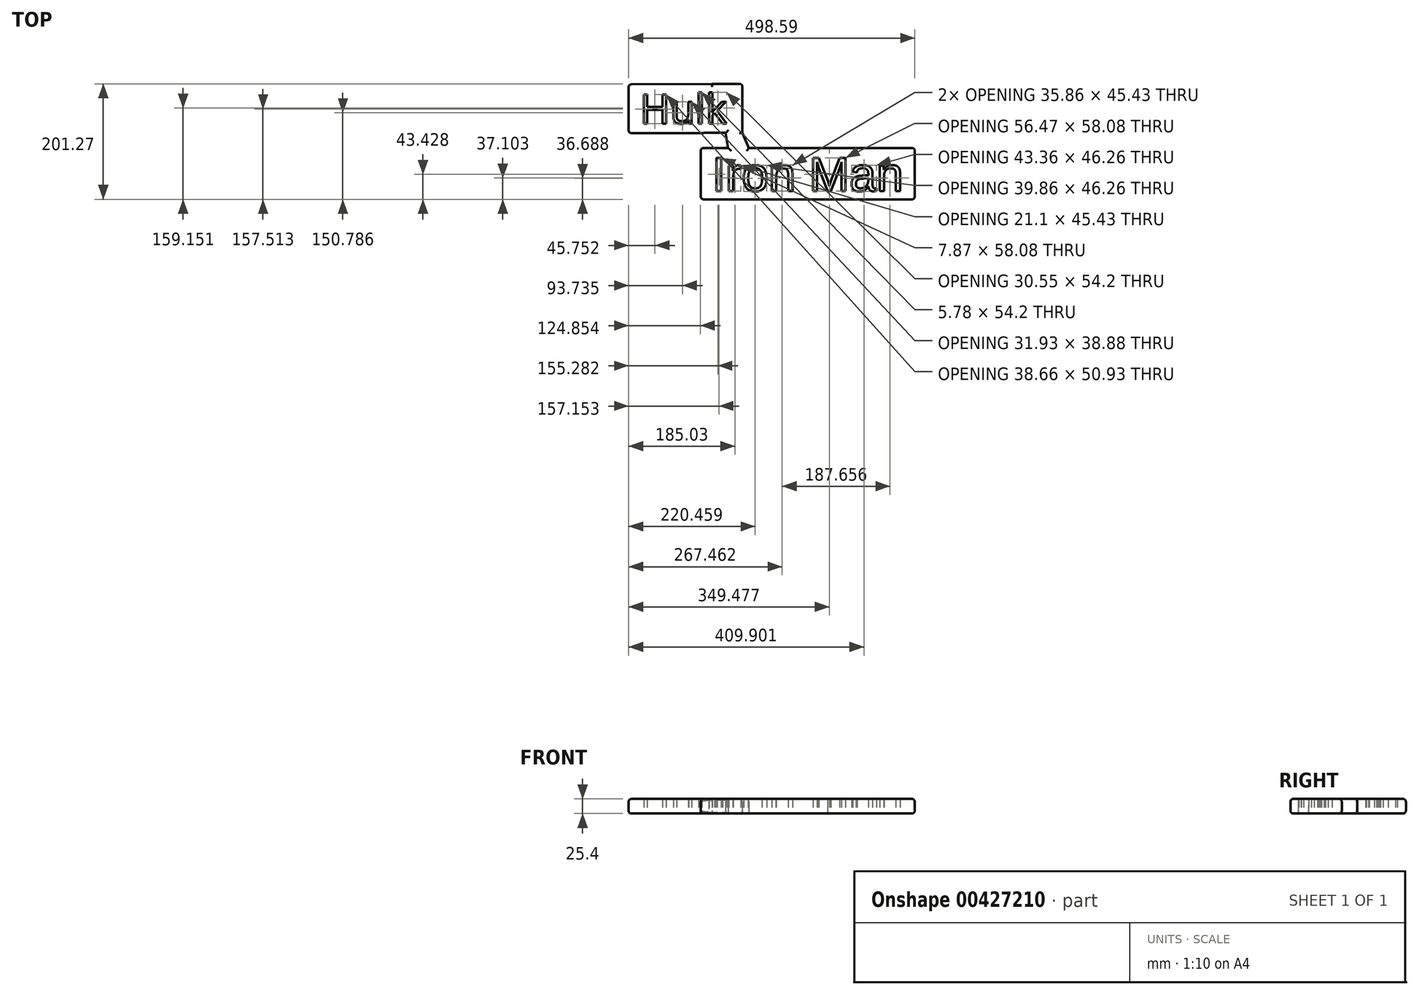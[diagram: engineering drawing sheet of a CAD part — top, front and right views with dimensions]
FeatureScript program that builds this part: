
annotation { "Feature Type Name" : "Feature", "Feature Type Description" : "" }
export const myFeature = defineFeature(function(context is Context, id is Id, definition is map)
    precondition{}
    {
        {
            var Q0;
            Q0=qCreatedBy(makeId("Top.planeOp"),FACE);
            var sketch = newSketch(context, id + "F0", { "sketchPlane" : qUnion([Q0])});
            skLineSegment(sketch, "E0", {"start": v(68.88, -39.62) * mm, "end": v(-56.84, -39.62) * mm});
            skLineSegment(sketch, "E1", {"start": v(-56.84, -39.62) * mm, "end": v(-56.84, 45.43) * mm});
            skLineSegment(sketch, "E2", {"start": v(-56.84, 45.43) * mm, "end": v(88.58, 46.24) * mm});
            skText(sketch, "E3", { "text": "Iron Man", "fontName": "Arimo-Regular.ttf"});
            skPoint(sketch, "E3.firstSnap0", {"position": v(88.58, 46.24) * mm});
            skPoint(sketch, "E4.end.orphan", {"position": v(326.73, 0) * mm});
            skLineSegment(sketch, "E5", {"start": v(295.08, 47.04) * mm, "end": v(296.03, 47.04) * mm});
            skText(sketch, "E6", { "text": "Hulk", "fontName": "OpenSans-Regular.ttf"});
            skPoint(sketch, "E7.start.orphan", {"position": v(234, 47.04) * mm});
            skLineSegment(sketch, "E8", {"start": v(88.58, 46.24) * mm, "end": v(141.43, 46.24) * mm});
            skLineSegment(sketch, "E9", {"start": v(141.43, 46.24) * mm, "end": v(141.43, -38.79) * mm});
            skLineSegment(sketch, "E10", {"start": v(141.43, -38.79) * mm, "end": v(82.89, -38.79) * mm});
            skLineSegment(sketch, "E11", {"start": v(68.88, -39.62) * mm, "end": v(82.89, -38.79) * mm});
            skLineSegment(sketch, "E12", {"start": v(112.16, -38.79) * mm, "end": v(118.33, -79.87) * mm});
            skLineSegment(sketch, "E13", {"start": v(118.33, -79.87) * mm, "end": v(141.43, -38.79) * mm});
            skLineSegment(sketch, "E14", {"start": v(141.43, -38.79) * mm, "end": v(158.58, -79.87) * mm});
            skLineSegment(sketch, "E15.bottom", {"start": v(68.88, -65.48) * mm, "end": v(441.75, -65.48) * mm});
            skLineSegment(sketch, "E15.top", {"start": v(68.88, -155.03) * mm, "end": v(441.75, -155.03) * mm});
            skLineSegment(sketch, "E15.left", {"start": v(68.88, -65.48) * mm, "end": v(68.88, -155.03) * mm});
            skLineSegment(sketch, "E15.right", {"start": v(441.75, -65.48) * mm, "end": v(441.75, -155.03) * mm});
            skPoint(sketch, "E15.middle", {"position": v(255.31, -110.25) * mm});
            const initialGuessF0  = {"E3": [0.08858, -0.14064, 1, 0, 0.06078], "E6": [-0.03742, -0.02298, 1, 0, 0.05136]};
            skSetInitialGuess(sketch, initialGuessF0);
            skSolve(sketch);
        }
        {
            var Q0;
            Q0 = qSketchRegion(id + "F0", true);
            extrude(context, id + "F1", {"entities" : qUnion([Q0]), "depth" : 25.4 * mm});
        }
        {
            var Q0;
            Q0=makeQuery(id+"F0.imprint","IMPRINT",FACE,{"disambiguationData":[TD([[makeQuery(id+"F0.imprint","IMPRINT",EDGE,{"derivedFrom":sQuery(id+"F0.wireOp",EDGE,"E3.sketch_text.stroke-25")}),1.0]])]});
            extrude(context, id + "F2", {"entities" : qUnion([Q0]), "depth" : 25.4 * mm});
        }
        {
            var Q0;
            Q0=makeQuery(id+"F0.imprint","IMPRINT",FACE,{"disambiguationData":[TD([[makeQuery(id+"F0.imprint","IMPRINT",EDGE,{"derivedFrom":sQuery(id+"F0.wireOp",EDGE,"E3.sketch_text.stroke-102")}),1.0]])]});
            extrude(context, id + "F3", {"entities" : qUnion([Q0]), "depth" : 25.4 * mm});
        }
        {
            var Q0;
            Q0=makeQuery(id+"F1.opExtrude","SWEPT_EDGE",EDGE,{"disambiguationData":[OSD([sQuery(id+"F0.wireOp",EDGE,"E8"),sQuery(id+"F0.wireOp",EDGE,"E9")])]});
            fillet(context, id + "F4", {"entities" : qUnion([Q0]), "radius" : 5.08 * mm, "tangentPropagation" : true, "allowEdgeOverflow" : false});
        }
        {
            var Q0;
            Q0=makeQuery(id+"F1.opExtrude","CAP_EDGE",EDGE,{"disambiguationData":[OSD([sQuery(id+"F0.wireOp",EDGE,"E1")])],"isStart":true});
            fillet(context, id + "F5", {"entities" : qUnion([Q0]), "radius" : 5.08 * mm, "tangentPropagation" : true, "allowEdgeOverflow" : false});
        }
        {
            var Q0;
            Q0=makeQuery(id+"F1.opExtrude","CAP_EDGE",EDGE,{"disambiguationData":[OSD([sQuery(id+"F0.wireOp",EDGE,"E1")])],"isStart":false});
            fillet(context, id + "F6", {"entities" : qUnion([Q0]), "radius" : 5.08 * mm, "tangentPropagation" : true, "allowEdgeOverflow" : false});
        }
        {
            var Q0;
            Q0=makeQuery(id+"F1.opExtrude","CAP_EDGE",EDGE,{"disambiguationData":[OSD([sQuery(id+"F0.wireOp",EDGE,"E2")])],"isStart":false});
            fillet(context, id + "F7", {"entities" : qUnion([Q0]), "radius" : 5.08 * mm, "tangentPropagation" : true, "allowEdgeOverflow" : false});
        }
        {
            var Q0;
            Q0=makeQuery(id+"F1.opExtrude","CAP_EDGE",EDGE,{"disambiguationData":[OSD([sQuery(id+"F0.wireOp",EDGE,"E9")])],"isStart":false});
            fillet(context, id + "F8", {"entities" : qUnion([Q0]), "radius" : 5.08 * mm, "tangentPropagation" : true, "allowEdgeOverflow" : false});
        }
        {
            var Q0;
            Q0=makeQuery(id+"F1.opExtrude","CAP_EDGE",EDGE,{"disambiguationData":[OSD([sQuery(id+"F0.wireOp",EDGE,"E0")])],"isStart":false});
            fillet(context, id + "F9", {"entities" : qUnion([Q0]), "radius" : 5.08 * mm, "tangentPropagation" : true, "allowEdgeOverflow" : false});
        }
        {
            var Q0;
            Q0=makeQuery(id+"F1.opExtrude","CAP_EDGE",EDGE,{"disambiguationData":[OSD([sQuery(id+"F0.wireOp",EDGE,"E14")])],"isStart":false});
            fillet(context, id + "F10", {"entities" : qUnion([Q0]), "radius" : 5.08 * mm, "tangentPropagation" : true, "allowEdgeOverflow" : false});
        }
        {
            var Q0;
            Q0=makeQuery(id+"F1.opExtrude","CAP_EDGE",EDGE,{"disambiguationData":[OSD([sQuery(id+"F0.wireOp",EDGE,"E14")])],"isStart":true});
            fillet(context, id + "F11", {"entities" : qUnion([Q0]), "radius" : 5.08 * mm, "tangentPropagation" : true, "allowEdgeOverflow" : false});
        }
        {
            var Q0;
            Q0=makeQuery(id+"F1.opExtrude","CAP_EDGE",EDGE,{"disambiguationData":[OSD([sQuery(id+"F0.wireOp",EDGE,"E12")])],"isStart":true});
            fillet(context, id + "F12", {"entities" : qUnion([Q0]), "radius" : 5.08 * mm, "tangentPropagation" : true, "allowEdgeOverflow" : false});
        }
        {
            var Q0;
            Q0=makeQuery(id+"F1.opExtrude","CAP_EDGE",EDGE,{"disambiguationData":[OSD([sQuery(id+"F0.wireOp",EDGE,"E12")])],"isStart":false});
            fillet(context, id + "F13", {"entities" : qUnion([Q0]), "radius" : 5.08 * mm, "tangentPropagation" : true, "allowEdgeOverflow" : false});
        }
        {
            var Q0;
            {var subQ0=sQuery(id+"F0.wireOp",EDGE,"E15.bottom");Q0=makeQuery(id+"F1.opExtrude","CAP_EDGE",EDGE,{"disambiguationData":[OSD([subQ0]),TDD([makeQuery(id+"F0.imprint","IMPRINT",EDGE,{"disambiguationData":[TD([[makeQuery(id+"F0.imprint","INTERSECT",VERTEX,{"derivedFrom":[subQ0,sQuery(id+"F0.wireOp",EDGE,"E15.left")]}),-1.0]])],"derivedFrom":subQ0})])],"isStart":true});}
            fillet(context, id + "F14", {"entities" : qUnion([Q0]), "radius" : 5.08 * mm, "tangentPropagation" : true, "allowEdgeOverflow" : false});
        }
        {
            var Q0;
            {var subQ0=sQuery(id+"F0.wireOp",EDGE,"E15.bottom");Q0=makeQuery(id+"F1.opExtrude","CAP_EDGE",EDGE,{"disambiguationData":[OSD([subQ0]),TDD([makeQuery(id+"F0.imprint","IMPRINT",EDGE,{"disambiguationData":[TD([[makeQuery(id+"F0.imprint","INTERSECT",VERTEX,{"derivedFrom":[subQ0,sQuery(id+"F0.wireOp",EDGE,"E15.left")]}),-1.0]])],"derivedFrom":subQ0})])],"isStart":false});}
            fillet(context, id + "F15", {"entities" : qUnion([Q0]), "radius" : 5.08 * mm, "tangentPropagation" : true, "allowEdgeOverflow" : false});
        }
        {
            var Q0;
            Q0=makeQuery(id+"F1.opExtrude","CAP_EDGE",EDGE,{"disambiguationData":[OSD([sQuery(id+"F0.wireOp",EDGE,"E15.left")])],"isStart":true});
            fillet(context, id + "F16", {"entities" : qUnion([Q0]), "radius" : 5.08 * mm, "tangentPropagation" : true, "allowEdgeOverflow" : false});
        }
        {
            var Q0;
            {var subQ0=sQuery(id+"F0.wireOp",EDGE,"E15.bottom");Q0=makeQuery(id+"F1.opExtrude","CAP_EDGE",EDGE,{"disambiguationData":[OSD([subQ0]),TDD([makeQuery(id+"F0.imprint","IMPRINT",EDGE,{"disambiguationData":[TD([[makeQuery(id+"F0.imprint","INTERSECT",VERTEX,{"derivedFrom":[subQ0,sQuery(id+"F0.wireOp",EDGE,"E15.right")]}),1.0]])],"derivedFrom":subQ0})])],"isStart":true});}
            fillet(context, id + "F17", {"entities" : qUnion([Q0]), "radius" : 5.08 * mm, "tangentPropagation" : true, "allowEdgeOverflow" : false});
        }
        {
            var Q0;
            {var subQ0=sQuery(id+"F0.wireOp",EDGE,"E15.bottom");Q0=makeQuery(id+"F1.opExtrude","CAP_EDGE",EDGE,{"disambiguationData":[OSD([subQ0]),TDD([makeQuery(id+"F0.imprint","IMPRINT",EDGE,{"disambiguationData":[TD([[makeQuery(id+"F0.imprint","INTERSECT",VERTEX,{"derivedFrom":[subQ0,sQuery(id+"F0.wireOp",EDGE,"E15.right")]}),1.0]])],"derivedFrom":subQ0})])],"isStart":false});}
            fillet(context, id + "F18", {"entities" : qUnion([Q0]), "radius" : 5.08 * mm, "tangentPropagation" : true, "allowEdgeOverflow" : false});
        }
        {
            var Q0;
            Q0=makeQuery(id+"F1.opExtrude","CAP_EDGE",EDGE,{"disambiguationData":[OSD([sQuery(id+"F0.wireOp",EDGE,"E15.right")])],"isStart":true});
            fillet(context, id + "F19", {"entities" : qUnion([Q0]), "radius" : 5.08 * mm, "tangentPropagation" : true, "allowEdgeOverflow" : false});
        }
        {
            var Q0;
            Q0=makeQuery(id+"F1.opExtrude","CAP_EDGE",EDGE,{"disambiguationData":[OSD([sQuery(id+"F0.wireOp",EDGE,"E15.top")])],"isStart":false});
            fillet(context, id + "F20", {"entities" : qUnion([Q0]), "radius" : 5.08 * mm, "tangentPropagation" : true, "allowEdgeOverflow" : false});
        }
    });
